# Revit family: HARMANN - MAXEE_HT - poziomy
name_source: partatom
category: Mechanical Equipment
units: mm (PartAtom-declared; Revit-internal decimal feet)

## family parameters
Classification = None
Cut with Voids When Loaded = No
Host = Face
Maintain Annotation Orientation = No
Part Type = Normal
Room Calculation Point = No
Round Connector Dimension = Use Diameter
Shared = No

## types (40) — shared parameters
Autor = https://www.archispace.com
Default Elevation = 1219.2 mm
Description = Kanałowy wentylator oddymiający
Klasa odporności ogniowej Tmax = 400 [oC/2h]
Lookup Table Name = MAXEE_HT
Manufacturer = Harmann Polska Sp. z o.o.
Temperatura pracy T = 60 °C
Zasilanie Częstotliwość Minimalna fmin = 20 Hz
Zasilanie Częstotliwość Nominalna fnom = 50 Hz
Zasilanie Ilość faz = 3
Zasilanie napięcie nominalne Unom = 400 V

## per-type parameters (varying)
- MAXEE.HT 315/4/3950T: A=380 mm; Akc ESD=HARMANN - Akcesoria - ESD : ESD 315; Akc FAL=HARMANN - Akcesoria - FAL : FAL 315; Akc FSD=HARMANN - Akcesoria - FSD : FSD 01; Akc RAF=HARMANN - Akcesoria - RAF : RAF 315; Akc RAS F4=HARMANN - Akcesoria - RAS F4 : RAS 315 F4; Akc RVK H F4=HARMANN - Akcesoria - RVK H F4 : RVK H 315 F4; Akc RVS=HARMANN - Akcesoria - RVS : RVS 315; Akc SGE=HARMANN - Akcesoria - SGE : SGE 315; Akc SGE dla ESD=HARMANN - Akcesoria - SGE : SGE 355; B=383 mm; C=355 mm; Ciśnienie akustyczne nominalne obudowa Lpa=58 dB(A); D=315 mm; D2=321 mm; Długość MAXEE=383 mm; F=396 mm; MAXEE_HT=HARMANN - MAXEE_HT : MAXEE.HT 315/4/3950T; Masa=23.10 kg; Moc akustyczna nominalna obudowa Lwa=65 dB(A); N1=1  [stored 0.00328084 ft]; Numer artykułu=15470200; Obroty nominalne nnom=1485.000 RPM; Powietrze Przepływ Maksymalny Qmax=3940.0 m³/h; Powietrze ciśnienie statyczne maksymalne dPmax=215.0 Pa; R2=157.5 mm; Wysokość=116.5 mm; Wysokość FAL=98 mm; Wysokość FSD=57 mm; Zasilanie Częstotliwość Maksymalna fmax=80 Hz; Zasilanie Moc maksymalna Pmax=174 W; Zasilanie natężenie maksymalne Imax=1 A
- MAXEE.HT 315/2/5800T: A=380 mm; Akc ESD=HARMANN - Akcesoria - ESD : ESD 315; Akc FAL=HARMANN - Akcesoria - FAL : FAL 315; Akc FSD=HARMANN - Akcesoria - FSD : FSD 01; Akc RAF=HARMANN - Akcesoria - RAF : RAF 315; Akc RAS F4=HARMANN - Akcesoria - RAS F4 : RAS 315 F4; Akc RVK H F4=HARMANN - Akcesoria - RVK H F4 : RVK H 315 F4; Akc RVS=HARMANN - Akcesoria - RVS : RVS 315; Akc SGE=HARMANN - Akcesoria - SGE : SGE 315; Akc SGE dla ESD=HARMANN - Akcesoria - SGE : SGE 355; B=383 mm; C=355 mm; Ciśnienie akustyczne nominalne obudowa Lpa=68 dB(A); D=315 mm; D2=321 mm; Długość MAXEE=383 mm; F=396 mm; MAXEE_HT=HARMANN - MAXEE_HT : MAXEE.HT 315/2/5800T; Masa=18.50 kg; Moc akustyczna nominalna obudowa Lwa=75 dB(A); N1=2  [stored 0.00656168 ft]; Numer artykułu=15470300; Obroty nominalne nnom=2880.000 RPM; Powietrze Przepływ Maksymalny Qmax=5810.0 m³/h; Powietrze ciśnienie statyczne maksymalne dPmax=490.0 Pa; R2=157.5 mm; Wysokość=116.5 mm; Wysokość FAL=98 mm; Wysokość FSD=57 mm; Zasilanie Częstotliwość Maksymalna fmax=60 Hz; Zasilanie Moc maksymalna Pmax=1386 W; Zasilanie natężenie maksymalne Imax=2 A
- MAXEE.HT 355/4/4900T: A=420 mm; Akc ESD=HARMANN - Akcesoria - ESD : ESD 355; Akc FAL=HARMANN - Akcesoria - FAL : FAL 355; Akc FSD=HARMANN - Akcesoria - FSD : FSD 01; Akc RAF=HARMANN - Akcesoria - RAF : RAF 355; Akc RAS F4=HARMANN - Akcesoria - RAS F4 : RAS 355 F4; Akc RVK H F4=HARMANN - Akcesoria - RVK H F4 : RVK H 355 F4; Akc RVS=HARMANN - Akcesoria - RVS : RVS 355; Akc SGE=HARMANN - Akcesoria - SGE : SGE 355; Akc SGE dla ESD=HARMANN - Akcesoria - SGE : SGE 400; B=383 mm; C=395 mm; Ciśnienie akustyczne nominalne obudowa Lpa=58 dB(A); D=355 mm; D2=361 mm; Długość MAXEE=383 mm; F=396 mm; MAXEE_HT=HARMANN - MAXEE_HT : MAXEE.HT 355/4/4900T; Masa=20.30 kg; Moc akustyczna nominalna obudowa Lwa=65 dB(A); N1=3  [stored 0.00984252 ft]; Numer artykułu=15470400; Obroty nominalne nnom=1480.000 RPM; Powietrze Przepływ Maksymalny Qmax=4870.0 m³/h; Powietrze ciśnienie statyczne maksymalne dPmax=230.0 Pa; R2=177.5 mm; Wysokość=136 mm; Wysokość FAL=99 mm; Wysokość FSD=57 mm; Zasilanie Częstotliwość Maksymalna fmax=70 Hz; Zasilanie Moc maksymalna Pmax=575 W; Zasilanie natężenie maksymalne Imax=1 A
- MAXEE.HT 355/2/6900T: A=420 mm; Akc ESD=HARMANN - Akcesoria - ESD : ESD 355; Akc FAL=HARMANN - Akcesoria - FAL : FAL 355; Akc FSD=HARMANN - Akcesoria - FSD : FSD 01; Akc RAF=HARMANN - Akcesoria - RAF : RAF 355; Akc RAS F4=HARMANN - Akcesoria - RAS F4 : RAS 355 F4; Akc RVK H F4=HARMANN - Akcesoria - RVK H F4 : RVK H 355 F4; Akc RVS=HARMANN - Akcesoria - RVS : RVS 355; Akc SGE=HARMANN - Akcesoria - SGE : SGE 355; Akc SGE dla ESD=HARMANN - Akcesoria - SGE : SGE 400; B=383 mm; C=395 mm; Ciśnienie akustyczne nominalne obudowa Lpa=66 dB(A); D=355 mm; D2=361 mm; Długość MAXEE=383 mm; F=396 mm; MAXEE_HT=HARMANN - MAXEE_HT : MAXEE.HT 355/2/6900T; Masa=24.10 kg; Moc akustyczna nominalna obudowa Lwa=73 dB(A); N1=4  [stored 0.0131234 ft]; Numer artykułu=15470500; Obroty nominalne nnom=2820.000 RPM; Powietrze Przepływ Maksymalny Qmax=6920.0 m³/h; Powietrze ciśnienie statyczne maksymalne dPmax=440.0 Pa; R2=177.5 mm; Wysokość=136 mm; Wysokość FAL=99 mm; Wysokość FSD=57 mm; Zasilanie Częstotliwość Maksymalna fmax=50 Hz; Zasilanie Moc maksymalna Pmax=1520 W; Zasilanie natężenie maksymalne Imax=2 A
- MAXEE.HT 400/4/6900T: A=480 mm; Akc ESD=HARMANN - Akcesoria - ESD : ESD 400; Akc FAL=HARMANN - Akcesoria - FAL : FAL 400; Akc FSD=HARMANN - Akcesoria - FSD : FSD 01; Akc RAF=HARMANN - Akcesoria - RAF : RAF 400; Akc RAS F4=HARMANN - Akcesoria - RAS F4 : RAS 400 F4; Akc RVK H F4=HARMANN - Akcesoria - RVK H F4 : RVK H 400 F4; Akc RVS=HARMANN - Akcesoria - RVS : RVS 400; Akc SGE=HARMANN - Akcesoria - SGE : SGE 400; Akc SGE dla ESD=HARMANN - Akcesoria - SGE : SGE 450; B=368 mm; C=450 mm; Ciśnienie akustyczne nominalne obudowa Lpa=62 dB(A); D=400 mm; D2=406 mm; Długość MAXEE=368 mm; F=396 mm; MAXEE_HT=HARMANN - MAXEE_HT : MAXEE.HT 400/4/6900T; Masa=27.10 kg; Moc akustyczna nominalna obudowa Lwa=69 dB(A); N1=5  [stored 0.0164042 ft]; Numer artykułu=15470600; Obroty nominalne nnom=1470.000 RPM; Powietrze Przepływ Maksymalny Qmax=6890.0 m³/h; Powietrze ciśnienie statyczne maksymalne dPmax=300.0 Pa; R2=200 mm; Wysokość=158.5 mm; Wysokość FAL=99 mm; Wysokość FSD=57 mm; Zasilanie Częstotliwość Maksymalna fmax=70 Hz; Zasilanie Moc maksymalna Pmax=1006 W; Zasilanie natężenie maksymalne Imax=1 A
- MAXEE.HT 400/2/10800T: A=480 mm; Akc ESD=HARMANN - Akcesoria - ESD : ESD 400; Akc FAL=HARMANN - Akcesoria - FAL : FAL 400; Akc FSD=HARMANN - Akcesoria - FSD : FSD 02; Akc RAF=HARMANN - Akcesoria - RAF : RAF 400; Akc RAS F4=HARMANN - Akcesoria - RAS F4 : RAS 400 F4; Akc RVK H F4=HARMANN - Akcesoria - RVK H F4 : RVK H 400 F4; Akc RVS=HARMANN - Akcesoria - RVS : RVS 400; Akc SGE=HARMANN - Akcesoria - SGE : SGE 400; Akc SGE dla ESD=HARMANN - Akcesoria - SGE : SGE 450; B=368 mm; C=450 mm; Ciśnienie akustyczne nominalne obudowa Lpa=70 dB(A); D=400 mm; D2=406 mm; Długość MAXEE=368 mm; F=396 mm; MAXEE_HT=HARMANN - MAXEE_HT : MAXEE.HT 400/2/10800T; Masa=34.10 kg; Moc akustyczna nominalna obudowa Lwa=77 dB(A); N1=6  [stored 0.019685 ft]; Numer artykułu=15470700; Obroty nominalne nnom=2865.000 RPM; Powietrze Przepływ Maksymalny Qmax=10820.0 m³/h; Powietrze ciśnienie statyczne maksymalne dPmax=750.0 Pa; R2=200 mm; Wysokość=158.5 mm; Wysokość FAL=99 mm; Wysokość FSD=57 mm; Zasilanie Częstotliwość Maksymalna fmax=55 Hz; Zasilanie Moc maksymalna Pmax=3497 W; Zasilanie natężenie maksymalne Imax=5 A
- MAXEE.HT 450/4/8500T: A=530 mm; Akc ESD=HARMANN - Akcesoria - ESD : ESD 450; Akc FAL=HARMANN - Akcesoria - FAL : FAL 450; Akc FSD=HARMANN - Akcesoria - FSD : FSD 02; Akc RAF=HARMANN - Akcesoria - RAF : RAF 450; Akc RAS F4=HARMANN - Akcesoria - RAS F4 : RAS 450 F4; Akc RVK H F4=HARMANN - Akcesoria - RVK H F4 : RVK H 450 F4; Akc RVS=HARMANN - Akcesoria - RVS : RVS 450; Akc SGE=HARMANN - Akcesoria - SGE : SGE 450; Akc SGE dla ESD=HARMANN - Akcesoria - SGE : SGE 500; B=368 mm; C=500 mm; Ciśnienie akustyczne nominalne obudowa Lpa=63 dB(A); D=450 mm; D2=456 mm; Długość MAXEE=368 mm; F=396 mm; MAXEE_HT=HARMANN - MAXEE_HT : MAXEE.HT 450/4/8500T; Masa=29.20 kg; Moc akustyczna nominalna obudowa Lwa=70 dB(A); N1=7  [stored 0.0229659 ft]; Numer artykułu=15470800; Obroty nominalne nnom=1450.000 RPM; Powietrze Przepływ Maksymalny Qmax=8460.0 m³/h; Powietrze ciśnienie statyczne maksymalne dPmax=280.0 Pa; R2=225 mm; Wysokość=183.5 mm; Wysokość FAL=99 mm; Wysokość FSD=57 mm; Zasilanie Częstotliwość Maksymalna fmax=60 Hz; Zasilanie Moc maksymalna Pmax=1129 W; Zasilanie natężenie maksymalne Imax=1 A
- MAXEE.HT 450/2/15300T: A=530 mm; Akc ESD=HARMANN - Akcesoria - ESD : ESD 450; Akc FAL=HARMANN - Akcesoria - FAL : FAL 450; Akc FSD=HARMANN - Akcesoria - FSD : FSD 01; Akc RAF=HARMANN - Akcesoria - RAF : RAF 450; Akc RAS F4=HARMANN - Akcesoria - RAS F4 : RAS 450 F4; Akc RVK H F4=HARMANN - Akcesoria - RVK H F4 : RVK H 450 F4; Akc RVS=HARMANN - Akcesoria - RVS : RVS 450; Akc SGE=HARMANN - Akcesoria - SGE : SGE 450; Akc SGE dla ESD=HARMANN - Akcesoria - SGE : SGE 500; B=368 mm; C=500 mm; Ciśnienie akustyczne nominalne obudowa Lpa=76 dB(A); D=450 mm; D2=456 mm; Długość MAXEE=368 mm; F=465 mm; MAXEE_HT=HARMANN - MAXEE_HT : MAXEE.HT 450/2/15300T; Masa=53.40 kg; Moc akustyczna nominalna obudowa Lwa=83 dB(A); N1=8  [stored 0.0262467 ft]; Numer artykułu=15470900; Obroty nominalne nnom=2910.000 RPM; Powietrze Przepływ Maksymalny Qmax=15300.0 m³/h; Powietrze ciśnienie statyczne maksymalne dPmax=960.0 Pa; R2=225 mm; Wysokość=183.5 mm; Wysokość FAL=99 mm; Wysokość FSD=57 mm; Zasilanie Częstotliwość Maksymalna fmax=55 Hz; Zasilanie Moc maksymalna Pmax=6325 W; Zasilanie natężenie maksymalne Imax=8 A
- MAXEE.HT 500/4/11600T: A=590 mm; Akc ESD=HARMANN - Akcesoria - ESD : ESD 500; Akc FAL=HARMANN - Akcesoria - FAL : FAL 500; Akc FSD=HARMANN - Akcesoria - FSD : FSD 02; Akc RAF=HARMANN - Akcesoria - RAF : RAF 500; Akc RAS F4=HARMANN - Akcesoria - RAS F4 : RAS 500 F4; Akc RVK H F4=HARMANN - Akcesoria - RVK H F4 : RVK H 500 F4; Akc RVS=HARMANN - Akcesoria - RVS : RVS 500; Akc SGE=HARMANN - Akcesoria - SGE : SGE 500; Akc SGE dla ESD=HARMANN - Akcesoria - SGE : SGE 560; B=443 mm; C=560 mm; Ciśnienie akustyczne nominalne obudowa Lpa=64 dB(A); D=500 mm; D2=506 mm; Długość MAXEE=443 mm; F=465 mm; MAXEE_HT=HARMANN - MAXEE_HT : MAXEE.HT 500/4/11600T; Masa=42.60 kg; Moc akustyczna nominalna obudowa Lwa=71 dB(A); N1=9  [stored 0.0295276 ft]; Numer artykułu=15471000; Obroty nominalne nnom=1465.000 RPM; Powietrze Przepływ Maksymalny Qmax=11640.0 m³/h; Powietrze ciśnienie statyczne maksymalne dPmax=360.0 Pa; R2=250 mm; Wysokość=208.5 mm; Wysokość FAL=99 mm; Wysokość FSD=57 mm; Zasilanie Częstotliwość Maksymalna fmax=60 Hz; Zasilanie Moc maksymalna Pmax=1817 W; Zasilanie natężenie maksymalne Imax=3 A
- MAXEE.HT 500/2/19600T: A=590 mm; Akc ESD=HARMANN - Akcesoria - ESD : ESD 500; Akc FAL=HARMANN - Akcesoria - FAL : FAL 500; Akc FSD=HARMANN - Akcesoria - FSD : FSD 02; Akc RAF=HARMANN - Akcesoria - RAF : RAF 500; Akc RAS F4=HARMANN - Akcesoria - RAS F4 : RAS 500 F4; Akc RVK H F4=HARMANN - Akcesoria - RVK H F4 : RVK H 500 F4; Akc RVS=HARMANN - Akcesoria - RVS : RVS 500; Akc SGE=HARMANN - Akcesoria - SGE : SGE 500; Akc SGE dla ESD=HARMANN - Akcesoria - SGE : SGE 560; B=443 mm; C=560 mm; Ciśnienie akustyczne nominalne obudowa Lpa=78 dB(A); D=500 mm; D2=506 mm; Długość MAXEE=443 mm; F=515 mm; MAXEE_HT=HARMANN - MAXEE_HT : MAXEE.HT 500/2/19600T; Masa=82.30 kg; Moc akustyczna nominalna obudowa Lwa=85 dB(A); N1=10  [stored 0.0328084 ft]; Numer artykułu=15471100; Obroty nominalne nnom=2940.000 RPM; Powietrze Przepływ Maksymalny Qmax=19630.0 m³/h; Powietrze ciśnienie statyczne maksymalne dPmax=970.0 Pa; R2=250 mm; Wysokość=208.5 mm; Wysokość FAL=99 mm; Wysokość FSD=57 mm; Zasilanie Częstotliwość Maksymalna fmax=50 Hz; Zasilanie Moc maksymalna Pmax=5928 W; Zasilanie natężenie maksymalne Imax=11 A
- MAXEE.HT 560/4/15400T: A=650 mm; Akc ESD=HARMANN - Akcesoria - ESD : ESD 560; Akc FAL=HARMANN - Akcesoria - FAL : FAL 560; Akc FSD=HARMANN - Akcesoria - FSD : FSD 03; Akc RAF=HARMANN - Akcesoria - RAF : RAF 560; Akc RAS F4=HARMANN - Akcesoria - RAS F4 : RAS 560 F4; Akc RVK H F4=HARMANN - Akcesoria - RVK H F4 : RVK H 560 F4; Akc RVS=HARMANN - Akcesoria - RVS : RVS 560; Akc SGE=HARMANN - Akcesoria - SGE : SGE 560; Akc SGE dla ESD=HARMANN - Akcesoria - SGE : SGE 630; B=443 mm; C=620 mm; Ciśnienie akustyczne nominalne obudowa Lpa=65 dB(A); D=560 mm; D2=566 mm; Długość MAXEE=443 mm; F=515 mm; MAXEE_HT=HARMANN - MAXEE_HT : MAXEE.HT 560/4/15400T; Masa=47.70 kg; Moc akustyczna nominalna obudowa Lwa=72 dB(A); N1=11  [stored 0.0360892 ft]; Numer artykułu=15471200; Obroty nominalne nnom=1450.000 RPM; Powietrze Przepływ Maksymalny Qmax=15380.0 m³/h; Powietrze ciśnienie statyczne maksymalne dPmax=350.0 Pa; R2=280 mm; Wysokość=238.5 mm; Wysokość FAL=99 mm; Wysokość FSD=57 mm; Zasilanie Częstotliwość Maksymalna fmax=55 Hz; Zasilanie Moc maksymalna Pmax=2577 W; Zasilanie natężenie maksymalne Imax=3 A
- MAXEE.HT 560/4/16600T: A=650 mm; Akc ESD=HARMANN - Akcesoria - ESD : ESD 560; Akc FAL=HARMANN - Akcesoria - FAL : FAL 560; Akc FSD=HARMANN - Akcesoria - FSD : FSD 02; Akc RAF=HARMANN - Akcesoria - RAF : RAF 560; Akc RAS F4=HARMANN - Akcesoria - RAS F4 : RAS 560 F4; Akc RVK H F4=HARMANN - Akcesoria - RVK H F4 : RVK H 560 F4; Akc RVS=HARMANN - Akcesoria - RVS : RVS 560; Akc SGE=HARMANN - Akcesoria - SGE : SGE 560; Akc SGE dla ESD=HARMANN - Akcesoria - SGE : SGE 630; B=443 mm; C=620 mm; Ciśnienie akustyczne nominalne obudowa Lpa=67 dB(A); D=560 mm; D2=566 mm; Długość MAXEE=443 mm; F=474 mm; MAXEE_HT=HARMANN - MAXEE_HT : MAXEE.HT 560/4/16600T; Masa=58.70 kg; Moc akustyczna nominalna obudowa Lwa=74 dB(A); N1=12  [stored 0.0393701 ft]; Numer artykułu=15471300; Obroty nominalne nnom=1455.000 RPM; Powietrze Przepływ Maksymalny Qmax=16580.0 m³/h; Powietrze ciśnienie statyczne maksymalne dPmax=430.0 Pa; R2=280 mm; Wysokość=238.5 mm; Wysokość FAL=99 mm; Wysokość FSD=57 mm; Zasilanie Częstotliwość Maksymalna fmax=60 Hz; Zasilanie Moc maksymalna Pmax=3162 W; Zasilanie natężenie maksymalne Imax=4 A
- MAXEE.HT 630/4/24600T: A=720 mm; Akc ESD=HARMANN - Akcesoria - ESD : ESD 630; Akc FAL=HARMANN - Akcesoria - FAL : FAL 630; Akc FSD=HARMANN - Akcesoria - FSD : FSD 02; Akc RAF=HARMANN - Akcesoria - RAF : RAF 630; Akc RAS F4=HARMANN - Akcesoria - RAS F4 : RAS 630 F4; Akc RVK H F4=HARMANN - Akcesoria - RVK H F4 : RVK H 630 F4; Akc RVS=HARMANN - Akcesoria - RVS : RVS 630; Akc SGE=HARMANN - Akcesoria - SGE : SGE 630; Akc SGE dla ESD=HARMANN - Akcesoria - SGE : SGE 710; B=443 mm; C=690 mm; Ciśnienie akustyczne nominalne obudowa Lpa=72 dB(A); D=630 mm; D2=636 mm; Długość MAXEE=443 mm; F=504 mm; MAXEE_HT=HARMANN - MAXEE_HT : MAXEE.HT 630/4/24600T; Masa=71.00 kg; Moc akustyczna nominalna obudowa Lwa=79 dB(A); N1=13  [stored 0.0426509 ft]; Numer artykułu=15471500; Obroty nominalne nnom=1470.000 RPM; Powietrze Przepływ Maksymalny Qmax=24620.0 m³/h; Powietrze ciśnienie statyczne maksymalne dPmax=625.0 Pa; R2=315 mm; Wysokość=273.5 mm; Wysokość FAL=99 mm; Wysokość FSD=57 mm; Zasilanie Częstotliwość Maksymalna fmax=65 Hz; Zasilanie Moc maksymalna Pmax=5680 W; Zasilanie natężenie maksymalne Imax=9 A
- MAXEE.HT 630/6/16200T: A=720 mm; Akc ESD=HARMANN - Akcesoria - ESD : ESD 630; Akc FAL=HARMANN - Akcesoria - FAL : FAL 630; Akc FSD=HARMANN - Akcesoria - FSD : FSD 02; Akc RAF=HARMANN - Akcesoria - RAF : RAF 630; Akc RAS F4=HARMANN - Akcesoria - RAS F4 : RAS 630 F4; Akc RVK H F4=HARMANN - Akcesoria - RVK H F4 : RVK H 630 F4; Akc RVS=HARMANN - Akcesoria - RVS : RVS 630; Akc SGE=HARMANN - Akcesoria - SGE : SGE 630; Akc SGE dla ESD=HARMANN - Akcesoria - SGE : SGE 710; B=443 mm; C=690 mm; Ciśnienie akustyczne nominalne obudowa Lpa=63 dB(A); D=630 mm; D2=636 mm; Długość MAXEE=443 mm; F=486 mm; MAXEE_HT=HARMANN - MAXEE_HT : MAXEE.HT 630/6/16200T; Masa=62.00 kg; Moc akustyczna nominalna obudowa Lwa=70 dB(A); N1=14  [stored 0.0459318 ft]; Numer artykułu=15471400; Obroty nominalne nnom=970.000 RPM; Powietrze Przepływ Maksymalny Qmax=16170.0 m³/h; Powietrze ciśnienie statyczne maksymalne dPmax=260.0 Pa; R2=315 mm; Wysokość=273.5 mm; Wysokość FAL=99 mm; Wysokość FSD=57 mm; Zasilanie Częstotliwość Maksymalna fmax=65 Hz; Zasilanie Moc maksymalna Pmax=1245 W; Zasilanie natężenie maksymalne Imax=3 A
- MAXEE.HT 710/6/22600T: A=810 mm; Akc ESD=HARMANN - Akcesoria - ESD : ESD 710; Akc FAL=HARMANN - Akcesoria - FAL : FAL 710; Akc FSD=HARMANN - Akcesoria - FSD : FSD 04; Akc RAF=HARMANN - Akcesoria - RAF : RAF 710; Akc RAS F4=HARMANN - Akcesoria - RAS F4 : RAS 710 F4; Akc RVK H F4=HARMANN - Akcesoria - RVK H F4 : RVK H 710 F4; Akc RVS=HARMANN - Akcesoria - RVS : RVS 710; Akc SGE=HARMANN - Akcesoria - SGE : SGE 710; Akc SGE dla ESD=HARMANN - Akcesoria - SGE : SGE 800; B=433 mm; C=770 mm; Ciśnienie akustyczne nominalne obudowa Lpa=66 dB(A); D=710 mm; D2=716 mm; Długość MAXEE=433 mm; F=600 mm; MAXEE_HT=HARMANN - MAXEE_HT : MAXEE.HT 710/6/22600T; Masa=78.80 kg; Moc akustyczna nominalna obudowa Lwa=73 dB(A); N1=15  [stored 0.0492126 ft]; Numer artykułu=15471600; Obroty nominalne nnom=980.000 RPM; Powietrze Przepływ Maksymalny Qmax=22570.0 m³/h; Powietrze ciśnienie statyczne maksymalne dPmax=320.0 Pa; R2=355 mm; Wysokość=303.5 mm; Wysokość FAL=119 mm; Wysokość FSD=57 mm; Zasilanie Częstotliwość Maksymalna fmax=60 Hz; Zasilanie Moc maksymalna Pmax=2212 W; Zasilanie natężenie maksymalne Imax=5 A
- MAXEE.HT 710/4/36600T: A=810 mm; Akc ESD=HARMANN - Akcesoria - ESD : ESD 710; Akc FAL=HARMANN - Akcesoria - FAL : FAL 710; Akc FSD=HARMANN - Akcesoria - FSD : FSD 04; Akc RAF=HARMANN - Akcesoria - RAF : RAF 710; Akc RAS F4=HARMANN - Akcesoria - RAS F4 : RAS 710 F4; Akc RVK H F4=HARMANN - Akcesoria - RVK H F4 : RVK H 710 F4; Akc RVS=HARMANN - Akcesoria - RVS : RVS 710; Akc SGE=HARMANN - Akcesoria - SGE : SGE 710; Akc SGE dla ESD=HARMANN - Akcesoria - SGE : SGE 800; B=433 mm; C=770 mm; Ciśnienie akustyczne nominalne obudowa Lpa=77 dB(A); D=710 mm; D2=716 mm; Długość MAXEE=433 mm; F=516 mm; MAXEE_HT=HARMANN - MAXEE_HT : MAXEE.HT 710/4/36600T; Masa=111.20 kg; Moc akustyczna nominalna obudowa Lwa=84 dB(A); N1=16  [stored 0.0524934 ft]; Numer artykułu=15471700; Obroty nominalne nnom=1480.000 RPM; Powietrze Przepływ Maksymalny Qmax=33670.0 m³/h; Powietrze ciśnienie statyczne maksymalne dPmax=715.0 Pa; R2=355 mm; Wysokość=303.5 mm; Wysokość FAL=119 mm; Wysokość FSD=57 mm; Zasilanie Częstotliwość Maksymalna fmax=60 Hz; Zasilanie Moc maksymalna Pmax=8500 W; Zasilanie natężenie maksymalne Imax=14 A
- MAXEE.HT 800/6/26500T: A=900 mm; Akc ESD=HARMANN - Akcesoria - ESD : ESD 800; Akc FAL=HARMANN - Akcesoria - FAL : FAL 800; Akc FSD=HARMANN - Akcesoria - FSD : FSD 10; Akc RAF=HARMANN - Akcesoria - RAF : RAF 800; Akc RAS F4=HARMANN - Akcesoria - RAS F4 : RAS 800 F4; Akc RVK H F4=HARMANN - Akcesoria - RVK H F4 : RVK H 800 F4; Akc RVS=HARMANN - Akcesoria - RVS : RVS 800; Akc SGE=HARMANN - Akcesoria - SGE : SGE 800; Akc SGE dla ESD=HARMANN - Akcesoria - SGE : SGE 900; B=648 mm; C=860 mm; Ciśnienie akustyczne nominalne obudowa Lpa=73 dB(A); D=800 mm; D2=806 mm; Długość MAXEE=648 mm; F=516 mm; MAXEE_HT=HARMANN - MAXEE_HT : MAXEE.HT 800/6/26500T; Masa=114.10 kg; Moc akustyczna nominalna obudowa Lwa=80 dB(A); N1=17  [stored 0.0557743 ft]; Numer artykułu=16246500; Obroty nominalne nnom=970.000 RPM; Powietrze Przepływ Maksymalny Qmax=26520.0 m³/h; Powietrze ciśnienie statyczne maksymalne dPmax=280.0 Pa; R2=400 mm; Wysokość=328 mm; Wysokość FAL=160 mm; Wysokość FSD=94 mm; Zasilanie Częstotliwość Maksymalna fmax=50 Hz; Zasilanie Moc maksymalna Pmax=3298 W; Zasilanie natężenie maksymalne Imax=5 A
- MAXEE.HT 800/4/30800T: A=900 mm; Akc ESD=HARMANN - Akcesoria - ESD : ESD 800; Akc FAL=HARMANN - Akcesoria - FAL : FAL 800; Akc FSD=HARMANN - Akcesoria - FSD : FSD 10; Akc RAF=HARMANN - Akcesoria - RAF : RAF 800; Akc RAS F4=HARMANN - Akcesoria - RAS F4 : RAS 800 F4; Akc RVK H F4=HARMANN - Akcesoria - RVK H F4 : RVK H 800 F4; Akc RVS=HARMANN - Akcesoria - RVS : RVS 800; Akc SGE=HARMANN - Akcesoria - SGE : SGE 800; Akc SGE dla ESD=HARMANN - Akcesoria - SGE : SGE 900; B=648 mm; C=860 mm; Ciśnienie akustyczne nominalne obudowa Lpa=74 dB(A); D=800 mm; D2=806 mm; Długość MAXEE=648 mm; F=516 mm; MAXEE_HT=HARMANN - MAXEE_HT : MAXEE.HT 800/4/30800T; Masa=117.10 kg; Moc akustyczna nominalna obudowa Lwa=81 dB(A); N1=18  [stored 0.0590551 ft]; Numer artykułu=16250700; Obroty nominalne nnom=1450.000 RPM; Powietrze Przepływ Maksymalny Qmax=30800.0 m³/h; Powietrze ciśnienie statyczne maksymalne dPmax=380.0 Pa; R2=400 mm; Wysokość=328 mm; Wysokość FAL=160 mm; Wysokość FSD=94 mm; Zasilanie Częstotliwość Maksymalna fmax=40 Hz; Zasilanie Moc maksymalna Pmax=3816 W; Zasilanie natężenie maksymalne Imax=10 A
- MAXEE.HT 800/4/31600T: A=900 mm; Akc ESD=HARMANN - Akcesoria - ESD : ESD 800; Akc FAL=HARMANN - Akcesoria - FAL : FAL 800; Akc FSD=HARMANN - Akcesoria - FSD : FSD 10; Akc RAF=HARMANN - Akcesoria - RAF : RAF 800; Akc RAS F4=HARMANN - Akcesoria - RAS F4 : RAS 800 F4; Akc RVK H F4=HARMANN - Akcesoria - RVK H F4 : RVK H 800 F4; Akc RVS=HARMANN - Akcesoria - RVS : RVS 800; Akc SGE=HARMANN - Akcesoria - SGE : SGE 800; Akc SGE dla ESD=HARMANN - Akcesoria - SGE : SGE 900; B=648 mm; C=860 mm; Ciśnienie akustyczne nominalne obudowa Lpa=74 dB(A); D=800 mm; D2=806 mm; Długość MAXEE=648 mm; F=516 mm; MAXEE_HT=HARMANN - MAXEE_HT : MAXEE.HT 800/4/31600T; Masa=142.10 kg; Moc akustyczna nominalna obudowa Lwa=81 dB(A); N1=19  [stored 0.062336 ft]; Numer artykułu=16252300; Obroty nominalne nnom=1450.000 RPM; Powietrze Przepływ Maksymalny Qmax=31640.0 m³/h; Powietrze ciśnienie statyczne maksymalne dPmax=780.0 Pa; R2=400 mm; Wysokość=328 mm; Wysokość FAL=160 mm; Wysokość FSD=94 mm; Zasilanie Częstotliwość Maksymalna fmax=40 Hz; Zasilanie Moc maksymalna Pmax=4780 W; Zasilanie natężenie maksymalne Imax=10 A
- MAXEE.HT 800/6/36800T: A=900 mm; Akc ESD=HARMANN - Akcesoria - ESD : ESD 800; Akc FAL=HARMANN - Akcesoria - FAL : FAL 800; Akc FSD=HARMANN - Akcesoria - FSD : FSD 10; Akc RAF=HARMANN - Akcesoria - RAF : RAF 800; Akc RAS F4=HARMANN - Akcesoria - RAS F4 : RAS 800 F4; Akc RVK H F4=HARMANN - Akcesoria - RVK H F4 : RVK H 800 F4; Akc RVS=HARMANN - Akcesoria - RVS : RVS 800; Akc SGE=HARMANN - Akcesoria - SGE : SGE 800; Akc SGE dla ESD=HARMANN - Akcesoria - SGE : SGE 900; B=648 mm; C=860 mm; Ciśnienie akustyczne nominalne obudowa Lpa=78 dB(A); D=800 mm; D2=806 mm; Długość MAXEE=648 mm; F=670 mm; MAXEE_HT=HARMANN - MAXEE_HT : MAXEE.HT 800/6/36800T; Masa=161.10 kg; Moc akustyczna nominalna obudowa Lwa=85 dB(A); N1=20  [stored 0.0656168 ft]; Numer artykułu=16254100; Obroty nominalne nnom=990.000 RPM; Powietrze Przepływ Maksymalny Qmax=36860.0 m³/h; Powietrze ciśnienie statyczne maksymalne dPmax=530.0 Pa; R2=400 mm; Wysokość=328 mm; Wysokość FAL=160 mm; Wysokość FSD=94 mm; Zasilanie Częstotliwość Maksymalna fmax=70 Hz; Zasilanie Moc maksymalna Pmax=6296 W; Zasilanie natężenie maksymalne Imax=12 A
- MAXEE.HT 800/4/39900T: A=900 mm; Akc ESD=HARMANN - Akcesoria - ESD : ESD 800; Akc FAL=HARMANN - Akcesoria - FAL : FAL 800; Akc FSD=HARMANN - Akcesoria - FSD : FSD 10; Akc RAF=HARMANN - Akcesoria - RAF : RAF 800; Akc RAS F4=HARMANN - Akcesoria - RAS F4 : RAS 800 F4; Akc RVK H F4=HARMANN - Akcesoria - RVK H F4 : RVK H 800 F4; Akc RVS=HARMANN - Akcesoria - RVS : RVS 800; Akc SGE=HARMANN - Akcesoria - SGE : SGE 800; Akc SGE dla ESD=HARMANN - Akcesoria - SGE : SGE 900; B=648 mm; C=860 mm; Ciśnienie akustyczne nominalne obudowa Lpa=81 dB(A); D=800 mm; D2=806 mm; Długość MAXEE=648 mm; F=670 mm; MAXEE_HT=HARMANN - MAXEE_HT : MAXEE.HT 800/4/39900T; Masa=153.10 kg; Moc akustyczna nominalna obudowa Lwa=88 dB(A); N1=21  [stored 0.0688976 ft]; Numer artykułu=16256200; Obroty nominalne nnom=1470.000 RPM; Powietrze Przepływ Maksymalny Qmax=39890.0 m³/h; Powietrze ciśnienie statyczne maksymalne dPmax=650.0 Pa; R2=400 mm; Wysokość=328 mm; Wysokość FAL=160 mm; Wysokość FSD=94 mm; Zasilanie Częstotliwość Maksymalna fmax=50 Hz; Zasilanie Moc maksymalna Pmax=7656 W; Zasilanie natężenie maksymalne Imax=15 A
- MAXEE.HT 800/4/48700T: A=900 mm; Akc ESD=HARMANN - Akcesoria - ESD : ESD 800; Akc FAL=HARMANN - Akcesoria - FAL : FAL 800; Akc FSD=HARMANN - Akcesoria - FSD : FSD 10; Akc RAF=HARMANN - Akcesoria - RAF : RAF 800; Akc RAS F4=HARMANN - Akcesoria - RAS F4 : RAS 800 F4; Akc RVK H F4=HARMANN - Akcesoria - RVK H F4 : RVK H 800 F4; Akc RVS=HARMANN - Akcesoria - RVS : RVS 800; Akc SGE=HARMANN - Akcesoria - SGE : SGE 800; Akc SGE dla ESD=HARMANN - Akcesoria - SGE : SGE 900; B=648 mm; C=860 mm; Ciśnienie akustyczne nominalne obudowa Lpa=82 dB(A); D=800 mm; D2=806 mm; Długość MAXEE=648 mm; F=725 mm; MAXEE_HT=HARMANN - MAXEE_HT : MAXEE.HT 800/4/48700T; Masa=186.10 kg; Moc akustyczna nominalna obudowa Lwa=89 dB(A); N1=22  [stored 0.0721785 ft]; Numer artykułu=16084400; Obroty nominalne nnom=1485.000 RPM; Powietrze Przepływ Maksymalny Qmax=48730.0 m³/h; Powietrze ciśnienie statyczne maksymalne dPmax=900.0 Pa; R2=400 mm; Wysokość=328 mm; Wysokość FAL=160 mm; Wysokość FSD=94 mm; Zasilanie Częstotliwość Maksymalna fmax=60 Hz; Zasilanie Moc maksymalna Pmax=9704 W; Zasilanie natężenie maksymalne Imax=24 A
- MAXEE.HT 900/4/43300T: A=1010 mm; Akc ESD=HARMANN - Akcesoria - ESD : ESD 900; Akc FAL=HARMANN - Akcesoria - FAL : FAL 900; Akc FSD=HARMANN - Akcesoria - FSD : FSD 10; Akc RAF=HARMANN - Akcesoria - RAF : RAF 900; Akc RAS F4=HARMANN - Akcesoria - RAS F4 : RAS 900 F4; Akc RVK H F4=HARMANN - Akcesoria - RVK H F4 : RVK H 900 F4; Akc RVS=HARMANN - Akcesoria - RVS : RVS 900; Akc SGE=HARMANN - Akcesoria - SGE : SGE 900; Akc SGE dla ESD=HARMANN - Akcesoria - SGE : SGE 1000; B=638 mm; C=970 mm; Ciśnienie akustyczne nominalne obudowa Lpa=77 dB(A); D=900 mm; D2=906 mm; Długość MAXEE=638 mm; F=725 mm; MAXEE_HT=HARMANN - MAXEE_HT : MAXEE.HT 900/4/43300T; Masa=158.20 kg; Moc akustyczna nominalna obudowa Lwa=84 dB(A); N1=23  [stored 0.0754593 ft]; Numer artykułu=16268500; Obroty nominalne nnom=1450.000 RPM; Powietrze Przepływ Maksymalny Qmax=43340.0 m³/h; Powietrze ciśnienie statyczne maksymalne dPmax=440.0 Pa; R2=450 mm; Wysokość=373 mm; Wysokość FAL=170 mm; Wysokość FSD=94 mm; Zasilanie Częstotliwość Maksymalna fmax=40 Hz; Zasilanie Moc maksymalna Pmax=6500 W; Zasilanie natężenie maksymalne Imax=15 A
- MAXEE.HT 900/6/43400T: A=1010 mm; Akc ESD=HARMANN - Akcesoria - ESD : ESD 900; Akc FAL=HARMANN - Akcesoria - FAL : FAL 900; Akc FSD=HARMANN - Akcesoria - FSD : FSD 10; Akc RAF=HARMANN - Akcesoria - RAF : RAF 900; Akc RAS F4=HARMANN - Akcesoria - RAS F4 : RAS 900 F4; Akc RVK H F4=HARMANN - Akcesoria - RVK H F4 : RVK H 900 F4; Akc RVS=HARMANN - Akcesoria - RVS : RVS 900; Akc SGE=HARMANN - Akcesoria - SGE : SGE 900; Akc SGE dla ESD=HARMANN - Akcesoria - SGE : SGE 1000; B=638 mm; C=970 mm; Ciśnienie akustyczne nominalne obudowa Lpa=76 dB(A); D=900 mm; D2=906 mm; Długość MAXEE=638 mm; F=695 mm; MAXEE_HT=HARMANN - MAXEE_HT : MAXEE.HT 900/6/43400T; Masa=177.20 kg; Moc akustyczna nominalna obudowa Lwa=83 dB(A); N1=24  [stored 0.0787402 ft]; Numer artykułu=16269100; Obroty nominalne nnom=980.000 RPM; Powietrze Przepływ Maksymalny Qmax=43390.0 m³/h; Powietrze ciśnienie statyczne maksymalne dPmax=990.0 Pa; R2=450 mm; Wysokość=373 mm; Wysokość FAL=170 mm; Wysokość FSD=94 mm; Zasilanie Częstotliwość Maksymalna fmax=60 Hz; Zasilanie Moc maksymalna Pmax=6601 W; Zasilanie natężenie maksymalne Imax=13 A
- MAXEE.HT 900/4/49400T: A=1010 mm; Akc ESD=HARMANN - Akcesoria - ESD : ESD 900; Akc FAL=HARMANN - Akcesoria - FAL : FAL 900; Akc FSD=HARMANN - Akcesoria - FSD : FSD 10; Akc RAF=HARMANN - Akcesoria - RAF : RAF 900; Akc RAS F4=HARMANN - Akcesoria - RAS F4 : RAS 900 F4; Akc RVK H F4=HARMANN - Akcesoria - RVK H F4 : RVK H 900 F4; Akc RVS=HARMANN - Akcesoria - RVS : RVS 900; Akc SGE=HARMANN - Akcesoria - SGE : SGE 900; Akc SGE dla ESD=HARMANN - Akcesoria - SGE : SGE 1000; B=638 mm; C=970 mm; Ciśnienie akustyczne nominalne obudowa Lpa=80 dB(A); D=900 mm; D2=906 mm; Długość MAXEE=638 mm; F=670 mm; MAXEE_HT=HARMANN - MAXEE_HT : MAXEE.HT 900/4/49400T; Masa=169.20 kg; Moc akustyczna nominalna obudowa Lwa=87 dB(A); N1=25  [stored 0.082021 ft]; Numer artykułu=16269700; Obroty nominalne nnom=1450.000 RPM; Powietrze Przepływ Maksymalny Qmax=49370.0 m³/h; Powietrze ciśnienie statyczne maksymalne dPmax=580.0 Pa; R2=450 mm; Wysokość=373 mm; Wysokość FAL=170 mm; Wysokość FSD=94 mm; Zasilanie Częstotliwość Maksymalna fmax=45 Hz; Zasilanie Moc maksymalna Pmax=9518 W; Zasilanie natężenie maksymalne Imax=18 A
- MAXEE.HT 900/4/54700T: A=1010 mm; Akc ESD=HARMANN - Akcesoria - ESD : ESD 900; Akc FAL=HARMANN - Akcesoria - FAL : FAL 900; Akc FSD=HARMANN - Akcesoria - FSD : FSD 10; Akc RAF=HARMANN - Akcesoria - RAF : RAF 900; Akc RAS F4=HARMANN - Akcesoria - RAS F4 : RAS 900 F4; Akc RVK H F4=HARMANN - Akcesoria - RVK H F4 : RVK H 900 F4; Akc RVS=HARMANN - Akcesoria - RVS : RVS 900; Akc SGE=HARMANN - Akcesoria - SGE : SGE 900; Akc SGE dla ESD=HARMANN - Akcesoria - SGE : SGE 1000; B=638 mm; C=970 mm; Ciśnienie akustyczne nominalne obudowa Lpa=83 dB(A); D=900 mm; D2=906 mm; Długość MAXEE=638 mm; F=750 mm; MAXEE_HT=HARMANN - MAXEE_HT : MAXEE.HT 900/4/54700T; Masa=200.80 kg; Moc akustyczna nominalna obudowa Lwa=90 dB(A); N1=26  [stored 0.0853018 ft]; Numer artykułu=16265600; Obroty nominalne nnom=1470.000 RPM; Powietrze Przepływ Maksymalny Qmax=54730.0 m³/h; Powietrze ciśnienie statyczne maksymalne dPmax=760.0 Pa; R2=450 mm; Wysokość=373 mm; Wysokość FAL=170 mm; Wysokość FSD=94 mm; Zasilanie Częstotliwość Maksymalna fmax=50 Hz; Zasilanie Moc maksymalna Pmax=13233 W; Zasilanie natężenie maksymalne Imax=25 A
- MAXEE.HT 900/4/60300T: A=1010 mm; Akc ESD=HARMANN - Akcesoria - ESD : ESD 900; Akc FAL=HARMANN - Akcesoria - FAL : FAL 900; Akc FSD=HARMANN - Akcesoria - FSD : FSD 10; Akc RAF=HARMANN - Akcesoria - RAF : RAF 900; Akc RAS F4=HARMANN - Akcesoria - RAS F4 : RAS 900 F4; Akc RVK H F4=HARMANN - Akcesoria - RVK H F4 : RVK H 900 F4; Akc RVS=HARMANN - Akcesoria - RVS : RVS 900; Akc SGE=HARMANN - Akcesoria - SGE : SGE 900; Akc SGE dla ESD=HARMANN - Akcesoria - SGE : SGE 1000; B=638 mm; C=970 mm; Ciśnienie akustyczne nominalne obudowa Lpa=77 dB(A); D=900 mm; D2=906 mm; Długość MAXEE=638 mm; F=794 mm; MAXEE_HT=HARMANN - MAXEE_HT : MAXEE.HT 900/4/60300T; Masa=244.80 kg; Moc akustyczna nominalna obudowa Lwa=90 dB(A); N1=27  [stored 0.0885827 ft]; Numer artykułu=16267900; Obroty nominalne nnom=1480.000 RPM; Powietrze Przepływ Maksymalny Qmax=60290.0 m³/h; Powietrze ciśnienie statyczne maksymalne dPmax=920.0 Pa; R2=450 mm; Wysokość=373 mm; Wysokość FAL=170 mm; Wysokość FSD=94 mm; Zasilanie Częstotliwość Maksymalna fmax=55 Hz; Zasilanie Moc maksymalna Pmax=17319 W; Zasilanie natężenie maksymalne Imax=31 A
- MAXEE.HT 1000/6/49300T: A=1110 mm; Akc ESD=HARMANN - Akcesoria - ESD : ESD 1000; Akc FAL=HARMANN - Akcesoria - FAL : FAL 1000; Akc FSD=HARMANN - Akcesoria - FSD : FSD 11; Akc RAF=HARMANN - Akcesoria - RAF : RAF 1000; Akc RAS F4=HARMANN - Akcesoria - RAS F4 : RAS 1000 F4; Akc RVK H F4=HARMANN - Akcesoria - RVK H F4 : RVK H 1000 F4; Akc RVS=HARMANN - Akcesoria - RVS : RVS 1000; Akc SGE=HARMANN - Akcesoria - SGE : SGE 1000; Akc SGE dla ESD=HARMANN - Akcesoria - SGE : SGE 1120; B=638 mm; C=1070 mm; Ciśnienie akustyczne nominalne obudowa Lpa=78 dB(A); D=1000 mm; D2=1006 mm; Długość MAXEE=638 mm; F=715 mm; MAXEE_HT=HARMANN - MAXEE_HT : MAXEE.HT 1000/6/49300T; Masa=195.00 kg; Moc akustyczna nominalna obudowa Lwa=85 dB(A); N1=28  [stored 0.0918635 ft]; Numer artykułu=16265000; Obroty nominalne nnom=970.000 RPM; Powietrze Przepływ Maksymalny Qmax=49290.0 m³/h; Powietrze ciśnienie statyczne maksymalne dPmax=400.0 Pa; R2=500 mm; Wysokość=383 mm; Wysokość FAL=250 mm; Wysokość FSD=94 mm; Zasilanie Częstotliwość Maksymalna fmax=50 Hz; Zasilanie Moc maksymalna Pmax=6663 W; Zasilanie natężenie maksymalne Imax=14 A
- MAXEE.HT 1000/4/60000T: A=1110 mm; Akc ESD=HARMANN - Akcesoria - ESD : ESD 1000; Akc FAL=HARMANN - Akcesoria - FAL : FAL 1000; Akc FSD=HARMANN - Akcesoria - FSD : FSD 11; Akc RAF=HARMANN - Akcesoria - RAF : RAF 1000; Akc RAS F4=HARMANN - Akcesoria - RAS F4 : RAS 1000 F4; Akc RVK H F4=HARMANN - Akcesoria - RVK H F4 : RVK H 1000 F4; Akc RVS=HARMANN - Akcesoria - RVS : RVS 1000; Akc SGE=HARMANN - Akcesoria - SGE : SGE 1000; Akc SGE dla ESD=HARMANN - Akcesoria - SGE : SGE 1120; B=638 mm; C=1070 mm; Ciśnienie akustyczne nominalne obudowa Lpa=78 dB(A); D=1000 mm; D2=1006 mm; Długość MAXEE=638 mm; F=770 mm; MAXEE_HT=HARMANN - MAXEE_HT : MAXEE.HT 1000/4/60000T; Masa=220.00 kg; Moc akustyczna nominalna obudowa Lwa=85 dB(A); N1=29  [stored 0.0951444 ft]; Numer artykułu=16260600; Obroty nominalne nnom=1450.000 RPM; Powietrze Przepływ Maksymalny Qmax=60040.0 m³/h; Powietrze ciśnienie statyczne maksymalne dPmax=600.0 Pa; R2=500 mm; Wysokość=383 mm; Wysokość FAL=250 mm; Wysokość FSD=94 mm; Zasilanie Częstotliwość Maksymalna fmax=40 Hz; Zasilanie Moc maksymalna Pmax=11300 W; Zasilanie natężenie maksymalne Imax=27 A
- MAXEE.HT 1000/6/60100T: A=1110 mm; Akc ESD=HARMANN - Akcesoria - ESD : ESD 1000; Akc FAL=HARMANN - Akcesoria - FAL : FAL 1000; Akc FSD=HARMANN - Akcesoria - FSD : FSD 11; Akc RAF=HARMANN - Akcesoria - RAF : RAF 1000; Akc RAS F4=HARMANN - Akcesoria - RAS F4 : RAS 1000 F4; Akc RVK H F4=HARMANN - Akcesoria - RVK H F4 : RVK H 1000 F4; Akc RVS=HARMANN - Akcesoria - RVS : RVS 1000; Akc SGE=HARMANN - Akcesoria - SGE : SGE 1000; Akc SGE dla ESD=HARMANN - Akcesoria - SGE : SGE 1120; B=638 mm; C=1070 mm; Ciśnienie akustyczne nominalne obudowa Lpa=78 dB(A); D=1000 mm; D2=1006 mm; Długość MAXEE=638 mm; F=814 mm; MAXEE_HT=HARMANN - MAXEE_HT : MAXEE.HT 1000/6/60100T; Masa=265.00 kg; Moc akustyczna nominalna obudowa Lwa=85 dB(A); N1=30  [stored 0.0984252 ft]; Numer artykułu=16262900; Obroty nominalne nnom=990.000 RPM; Powietrze Przepływ Maksymalny Qmax=60140.0 m³/h; Powietrze ciśnienie statyczne maksymalne dPmax=610.0 Pa; R2=500 mm; Wysokość=383 mm; Wysokość FAL=250 mm; Wysokość FSD=94 mm; Zasilanie Częstotliwość Maksymalna fmax=60 Hz; Zasilanie Moc maksymalna Pmax=15647 W; Zasilanie natężenie maksymalne Imax=22 A
- MAXEE.HT 1000/4/67500T: A=1110 mm; Akc ESD=HARMANN - Akcesoria - ESD : ESD 1000; Akc FAL=HARMANN - Akcesoria - FAL : FAL 1000; Akc FSD=HARMANN - Akcesoria - FSD : FSD 11; Akc RAF=HARMANN - Akcesoria - RAF : RAF 1000; Akc RAS F4=HARMANN - Akcesoria - RAS F4 : RAS 1000 F4; Akc RVK H F4=HARMANN - Akcesoria - RVK H F4 : RVK H 1000 F4; Akc RVS=HARMANN - Akcesoria - RVS : RVS 1000; Akc SGE=HARMANN - Akcesoria - SGE : SGE 1000; Akc SGE dla ESD=HARMANN - Akcesoria - SGE : SGE 1120; B=638 mm; C=1070 mm; Ciśnienie akustyczne nominalne obudowa Lpa=82 dB(A); D=1000 mm; D2=1006 mm; Długość MAXEE=638 mm; F=814 mm; MAXEE_HT=HARMANN - MAXEE_HT : MAXEE.HT 1000/4/67500T; Masa=264.00 kg; Moc akustyczna nominalna obudowa Lwa=89 dB(A); N1=31  [stored 0.101706 ft]; Numer artykułu=16263400; Obroty nominalne nnom=1450.000 RPM; Powietrze Przepływ Maksymalny Qmax=67550.0 m³/h; Powietrze ciśnienie statyczne maksymalne dPmax=1160.0 Pa; R2=500 mm; Wysokość=383 mm; Wysokość FAL=250 mm; Wysokość FSD=94 mm; Zasilanie Częstotliwość Maksymalna fmax=45 Hz; Zasilanie Moc maksymalna Pmax=16042 W; Zasilanie natężenie maksymalne Imax=33 A
- MAXEE.HT 1000/4/75800T: A=1110 mm; Akc ESD=HARMANN - Akcesoria - ESD : ESD 1000; Akc FAL=HARMANN - Akcesoria - FAL : FAL 1000; Akc FSD=HARMANN - Akcesoria - FSD : FSD 11; Akc RAF=HARMANN - Akcesoria - RAF : RAF 1000; Akc RAS F4=HARMANN - Akcesoria - RAS F4 : RAS 1000 F4; Akc RVK H F4=HARMANN - Akcesoria - RVK H F4 : RVK H 1000 F4; Akc RVS=HARMANN - Akcesoria - RVS : RVS 1000; Akc SGE=HARMANN - Akcesoria - SGE : SGE 1000; Akc SGE dla ESD=HARMANN - Akcesoria - SGE : SGE 1120; B=638 mm; C=1070 mm; Ciśnienie akustyczne nominalne obudowa Lpa=84 dB(A); D=1000 mm; D2=1006 mm; Długość MAXEE=638 mm; F=872 mm; MAXEE_HT=HARMANN - MAXEE_HT : MAXEE.HT 1000/4/75800T; Masa=313.00 kg; Moc akustyczna nominalna obudowa Lwa=91 dB(A); N1=32  [stored 0.104987 ft]; Numer artykułu=16264500; Obroty nominalne nnom=1480.000 RPM; Powietrze Przepływ Maksymalny Qmax=75810.0 m³/h; Powietrze ciśnienie statyczne maksymalne dPmax=980.0 Pa; R2=500 mm; Wysokość=383 mm; Wysokość FAL=250 mm; Wysokość FSD=94 mm; Zasilanie Częstotliwość Maksymalna fmax=50 Hz; Zasilanie Moc maksymalna Pmax=22034 W; Zasilanie natężenie maksymalne Imax=41 A
- MAXEE.HT 1000/4/76100T: A=1110 mm; Akc ESD=HARMANN - Akcesoria - ESD : ESD 1000; Akc FAL=HARMANN - Akcesoria - FAL : FAL 1000; Akc FSD=HARMANN - Akcesoria - FSD : FSD 11; Akc RAF=HARMANN - Akcesoria - RAF : RAF 1000; Akc RAS F4=HARMANN - Akcesoria - RAS F4 : RAS 1000 F4; Akc RVK H F4=HARMANN - Akcesoria - RVK H F4 : RVK H 1000 F4; Akc RVS=HARMANN - Akcesoria - RVS : RVS 1000; Akc SGE=HARMANN - Akcesoria - SGE : SGE 1000; Akc SGE dla ESD=HARMANN - Akcesoria - SGE : SGE 1120; B=638 mm; C=1070 mm; Ciśnienie akustyczne nominalne obudowa Lpa=87 dB(A); D=1000 mm; D2=1006 mm; Długość MAXEE=638 mm; F=834 mm; MAXEE_HT=HARMANN - MAXEE_HT : MAXEE.HT 1000/4/76100T; Masa=280.00 kg; Moc akustyczna nominalna obudowa Lwa=94 dB(A); N1=33  [stored 0.108268 ft]; Numer artykułu=16263900; Obroty nominalne nnom=1480.000 RPM; Powietrze Przepływ Maksymalny Qmax=76100.0 m³/h; Powietrze ciśnienie statyczne maksymalne dPmax=970.0 Pa; R2=500 mm; Wysokość=383 mm; Wysokość FAL=250 mm; Wysokość FSD=94 mm; Zasilanie Częstotliwość Maksymalna fmax=50 Hz; Zasilanie Moc maksymalna Pmax=23206 W; Zasilanie natężenie maksymalne Imax=41 A
- MAXEE.HT 1120/6/62200T: A=1240 mm; Akc ESD=HARMANN - Akcesoria - ESD : ESD 1120; Akc FAL=HARMANN - Akcesoria - FAL : FAL 1120; Akc FSD=HARMANN - Akcesoria - FSD : FSD 11; Akc RAF=HARMANN - Akcesoria - RAF : RAF 1120; Akc RAS F4=HARMANN - Akcesoria - RAS F4 : RAS 1120 F4; Akc RVK H F4=HARMANN - Akcesoria - RVK H F4 : RVK H 1120 F4; Akc RVS=HARMANN - Akcesoria - RVS : RVS 1120; Akc SGE=HARMANN - Akcesoria - SGE : SGE 1120; Akc SGE dla ESD=HARMANN - Akcesoria - SGE : SGE 1250; B=728 mm; C=1190 mm; Ciśnienie akustyczne nominalne obudowa Lpa=80 dB(A); D=1120 mm; D2=1126 mm; Długość MAXEE=728 mm; F=745 mm; MAXEE_HT=HARMANN - MAXEE_HT : MAXEE.HT 1120/6/62200T; Masa=218.00 kg; Moc akustyczna nominalna obudowa Lwa=87 dB(A); N1=34  [stored 0.111549 ft]; Numer artykułu=16271300; Obroty nominalne nnom=980.000 RPM; Powietrze Przepływ Maksymalny Qmax=62250.0 m³/h; Powietrze ciśnienie statyczne maksymalne dPmax=390.0 Pa; R2=560 mm; Wysokość=433 mm; Wysokość FAL=270 mm; Wysokość FSD=94 mm; Zasilanie Częstotliwość Maksymalna fmax=45 Hz; Zasilanie Moc maksymalna Pmax=7053 W; Zasilanie natężenie maksymalne Imax=16 A
- MAXEE.HT 1120/6/71400T: A=1240 mm; Akc ESD=HARMANN - Akcesoria - ESD : ESD 1120; Akc FAL=HARMANN - Akcesoria - FAL : FAL 1120; Akc FSD=HARMANN - Akcesoria - FSD : FSD 11; Akc RAF=HARMANN - Akcesoria - RAF : RAF 1120; Akc RAS F4=HARMANN - Akcesoria - RAS F4 : RAS 1120 F4; Akc RVK H F4=HARMANN - Akcesoria - RVK H F4 : RVK H 1120 F4; Akc RVS=HARMANN - Akcesoria - RVS : RVS 1120; Akc SGE=HARMANN - Akcesoria - SGE : SGE 1120; Akc SGE dla ESD=HARMANN - Akcesoria - SGE : SGE 1250; B=728 mm; C=1190 mm; Ciśnienie akustyczne nominalne obudowa Lpa=86 dB(A); D=1120 mm; D2=1126 mm; Długość MAXEE=728 mm; F=844 mm; MAXEE_HT=HARMANN - MAXEE_HT : MAXEE.HT 1120/6/71400T; Masa=298.00 kg; Moc akustyczna nominalna obudowa Lwa=93 dB(A); N1=35  [stored 0.114829 ft]; Numer artykułu=16270400; Obroty nominalne nnom=980.000 RPM; Powietrze Przepływ Maksymalny Qmax=71380.0 m³/h; Powietrze ciśnienie statyczne maksymalne dPmax=545.0 Pa; R2=560 mm; Wysokość=433 mm; Wysokość FAL=270 mm; Wysokość FSD=94 mm; Zasilanie Częstotliwość Maksymalna fmax=50 Hz; Zasilanie Moc maksymalna Pmax=12903 W; Zasilanie natężenie maksymalne Imax=24 A
- MAXEE.HT 1120/6/85800T: A=1240 mm; Akc ESD=HARMANN - Akcesoria - ESD : ESD 1120; Akc FAL=HARMANN - Akcesoria - FAL : FAL 1120; Akc FSD=HARMANN - Akcesoria - FSD : FSD 11; Akc RAF=HARMANN - Akcesoria - RAF : RAF 1120; Akc RAS F4=HARMANN - Akcesoria - RAS F4 : RAS 1120 F4; Akc RVK H F4=HARMANN - Akcesoria - RVK H F4 : RVK H 1120 F4; Akc RVS=HARMANN - Akcesoria - RVS : RVS 1120; Akc SGE=HARMANN - Akcesoria - SGE : SGE 1120; Akc SGE dla ESD=HARMANN - Akcesoria - SGE : SGE 1250; B=728 mm; C=1190 mm; Ciśnienie akustyczne nominalne obudowa Lpa=87 dB(A); D=1120 mm; D2=1126 mm; Długość MAXEE=728 mm; F=967 mm; MAXEE_HT=HARMANN - MAXEE_HT : MAXEE.HT 1120/6/85800T; Masa=345.00 kg; Moc akustyczna nominalna obudowa Lwa=94 dB(A); N1=36  [stored 0.11811 ft]; Numer artykułu=16270900; Obroty nominalne nnom=990.000 RPM; Powietrze Przepływ Maksymalny Qmax=85820.0 m³/h; Powietrze ciśnienie statyczne maksymalne dPmax=765.0 Pa; R2=560 mm; Wysokość=433 mm; Wysokość FAL=270 mm; Wysokość FSD=94 mm; Zasilanie Częstotliwość Maksymalna fmax=60 Hz; Zasilanie Moc maksymalna Pmax=20147 W; Zasilanie natężenie maksymalne Imax=38 A
- MAXEE.HT 1250/6/79400T: A=1370 mm; Akc ESD=HARMANN - Akcesoria - ESD : ESD 1250; Akc FAL=HARMANN - Akcesoria - FAL : FAL 1250; Akc FSD=HARMANN - Akcesoria - FSD : FSD 11; Akc RAF=HARMANN - Akcesoria - RAF : RAF 1250; Akc RAS F4=HARMANN - Akcesoria - RAS F4 : RAS 1250 F4; Akc RVK H F4=HARMANN - Akcesoria - RVK H F4 : RVK H 1250 F4; Akc RVS=HARMANN - Akcesoria - RVS : RVS 1250; Akc SGE=HARMANN - Akcesoria - SGE : SGE 1250; Akc SGE dla ESD=HARMANN - Akcesoria - SGE : SGE 1400; B=728 mm; C=1320 mm; Ciśnienie akustyczne nominalne obudowa Lpa=80 dB(A); D=1250 mm; D2=1256 mm; Długość MAXEE=728 mm; F=874 mm; MAXEE_HT=HARMANN - MAXEE_HT : MAXEE.HT 1250/6/79400T; Masa=280.00 kg; Moc akustyczna nominalna obudowa Lwa=87 dB(A); N1=37  [stored 0.121391 ft]; Numer artykułu=16256800; Obroty nominalne nnom=980.000 RPM; Powietrze Przepływ Maksymalny Qmax=79450.0 m³/h; Powietrze ciśnienie statyczne maksymalne dPmax=420.0 Pa; R2=625 mm; Wysokość=498 mm; Wysokość FAL=270 mm; Wysokość FSD=94 mm; Zasilanie Częstotliwość Maksymalna fmax=40 Hz; Zasilanie Moc maksymalna Pmax=10850 W; Zasilanie natężenie maksymalne Imax=26 A
- MAXEE.HT 1250/6/98500T: A=1370 mm; Akc ESD=HARMANN - Akcesoria - ESD : ESD 1250; Akc FAL=HARMANN - Akcesoria - FAL : FAL 1250; Akc FSD=HARMANN - Akcesoria - FSD : FSD 11; Akc RAF=HARMANN - Akcesoria - RAF : RAF 1250; Akc RAS F4=HARMANN - Akcesoria - RAS F4 : RAS 1250 F4; Akc RVK H F4=HARMANN - Akcesoria - RVK H F4 : RVK H 1250 F4; Akc RVS=HARMANN - Akcesoria - RVS : RVS 1250; Akc SGE=HARMANN - Akcesoria - SGE : SGE 1250; Akc SGE dla ESD=HARMANN - Akcesoria - SGE : SGE 1400; B=728 mm; C=1320 mm; Ciśnienie akustyczne nominalne obudowa Lpa=89 dB(A); D=1250 mm; D2=1256 mm; Długość MAXEE=728 mm; F=997 mm; MAXEE_HT=HARMANN - MAXEE_HT : MAXEE.HT 1250/6/98500T; Masa=365.00 kg; Moc akustyczna nominalna obudowa Lwa=96 dB(A); N1=38  [stored 0.124672 ft]; Numer artykułu=16257600; Obroty nominalne nnom=980.000 RPM; Powietrze Przepływ Maksymalny Qmax=98520.0 m³/h; Powietrze ciśnienie statyczne maksymalne dPmax=670.0 Pa; R2=625 mm; Wysokość=498 mm; Wysokość FAL=270 mm; Wysokość FSD=94 mm; Zasilanie Częstotliwość Maksymalna fmax=50 Hz; Zasilanie Moc maksymalna Pmax=21529 W; Zasilanie natężenie maksymalne Imax=41 A
- MAXEE.HT 1250/6/109300T: A=1370 mm; Akc ESD=HARMANN - Akcesoria - ESD : ESD 1250; Akc FAL=HARMANN - Akcesoria - FAL : FAL 1250; Akc FSD=HARMANN - Akcesoria - FSD : FSD 11; Akc RAF=HARMANN - Akcesoria - RAF : RAF 1250; Akc RAS F4=HARMANN - Akcesoria - RAS F4 : RAS 1250 F4; Akc RVK H F4=HARMANN - Akcesoria - RVK H F4 : RVK H 1250 F4; Akc RVS=HARMANN - Akcesoria - RVS : RVS 1250; Akc SGE=HARMANN - Akcesoria - SGE : SGE 1250; Akc SGE dla ESD=HARMANN - Akcesoria - SGE : SGE 1250; B=728 mm; C=1320 mm; Ciśnienie akustyczne nominalne obudowa Lpa=88 dB(A); D=1250 mm; D2=1256 mm; Długość MAXEE=728 mm; F=997 mm; MAXEE_HT=HARMANN - MAXEE_HT : MAXEE.HT 1250/6/109300T; Masa=376.00 kg; Moc akustyczna nominalna obudowa Lwa=95 dB(A); N1=39  [stored 0.127953 ft]; Numer artykułu=16258100; Obroty nominalne nnom=980.000 RPM; Powietrze Przepływ Maksymalny Qmax=109260.0 m³/h; Powietrze ciśnienie statyczne maksymalne dPmax=835.0 Pa; R2=625 mm; Wysokość=498 mm; Wysokość FAL=270 mm; Wysokość FSD=94 mm; Zasilanie Częstotliwość Maksymalna fmax=55 Hz; Zasilanie Moc maksymalna Pmax=28129 W; Zasilanie natężenie maksymalne Imax=52 A
- MAXEE.HT 1250/6/119600T: A=1370 mm; Akc ESD=HARMANN - Akcesoria - ESD : ESD 1250; Akc FAL=HARMANN - Akcesoria - FAL : FAL 1250; Akc FSD=HARMANN - Akcesoria - FSD : FSD 11; Akc RAF=HARMANN - Akcesoria - RAF : RAF 1250; Akc RAS F4=HARMANN - Akcesoria - RAS F4 : RAS 1250 F4; Akc RVK H F4=HARMANN - Akcesoria - RVK H F4 : RVK H 1250 F4; Akc RVS=HARMANN - Akcesoria - RVS : RVS 1250; Akc SGE=HARMANN - Akcesoria - SGE : SGE 1250; Akc SGE dla ESD=HARMANN - Akcesoria - SGE : SGE 1400; B=728 mm; C=1320 mm; Ciśnienie akustyczne nominalne obudowa Lpa=89 dB(A); D=1250 mm; D2=1256 mm; Długość MAXEE=728 mm; F=997 mm; MAXEE_HT=HARMANN - MAXEE_HT : MAXEE.HT 1250/6/119600T; Masa=550.00 kg; Moc akustyczna nominalna obudowa Lwa=96 dB(A); N1=40  [stored 0.131234 ft]; Numer artykułu=16259000; Obroty nominalne nnom=990.000 RPM; Powietrze Przepływ Maksymalny Qmax=119640.0 m³/h; Powietrze ciśnienie statyczne maksymalne dPmax=1015.0 Pa; R2=625 mm; Wysokość=498 mm; Wysokość FAL=270 mm; Wysokość FSD=94 mm; Zasilanie Częstotliwość Maksymalna fmax=60 Hz; Zasilanie Moc maksymalna Pmax=37683 W; Zasilanie natężenie maksymalne Imax=69 A

note: column(s) folded — value = type name in every type: Model

note: [stored X ft] marks values corroborated as IEEE doubles in the binary element streams (Revit-internal decimal feet)

## geometry (parser evidence)
native form markers: Sweep x29
no freeform markers — native parametric forms only
